# Revit family: V-LENSESxx102xxWSxx
name_source: partatom
category: Leuchten
units: mm (PartAtom-declared; Revit-internal decimal feet)

## family parameters
Basisbauteil = Fläche
Beim Laden mit Abzugskörper schneiden = Nein
Bemaßung runder Anschluss = Durchmesser verwenden
Gemeinsam genutzt = Nein
Lichtquelle = Ja
OmniClass-Nummer = 23.80.70.11
OmniClass-Titel = Luminaries for Internal Lighting
Raumberechnungspunkt = Nein
Teiletyp = Normal

## types (8) — shared parameters
Baugruppenkennzeichen = D5020200
Emissionsform beim Rendern sichtbar = Nein
Farbfilter = 16777215
Farbtemperaturverschiebung bei Dämpfen der Lampe = <Keine Auswahl>
Hersteller = RIDI Leuchten GmbH
Lampe = LED
Neigungswinkel = 90.00°
URL = www.ridi.de
Von Breite des Rechtecks ausssenden = 1018 mm  [stored 3.3399 ft]
Von Länge des Rechtecks aussenden = 111 mm
brand = RIDI
conformity mark = CE
electrical safety class = 1
height = 83 mm  [stored 0.27231 ft]
ingress protection (IP) code = IP20
length = 1024 mm  [stored 3.35958 ft]
nominal frequency = 50-60Hz
nominal voltage = 230
voltage type (AC, DC, UC) = AC
width = 113 mm  [stored 0.370735 ft]
zero-valued in all types: Vorgabe-Ansicht

## per-type parameters (varying)
| type | Datei für fotometrisches Netz | Modell | Scheinlast | product name | rated input power | weight |
| V-LENSES-D102-5RFWS840B0450 | V-LENSES-D.IES | 1522559 | 26 VA | V-LENSES-D102-5RFWS840B0450
V-LENSES-DI102-7DASW830B0550 | 26 | 2,6 |
| V-LENSES-D102-7DAWS830B0350 | V-LENSES-D.IES | 1532563 | 22 VA | V-LENSES-D102-7DAWS830B0350
V-LENSES-DI102-7DASW830B0550 | 22 | 2,6 |
| V-LENSES-D102-7DAWS840B0350 | V-LENSES-D.IES | 1532555 | 22 VA | V-LENSES-D102-7DAWS840B0350
V-LENSES-DI102-7DASW830B0550 | 22 | 2,6 |
| V-LENSES-DI102-5RFWS830B0500 | V-LENSES-DI.IES | 1522568 | 37 VA | V-LENSES-DI102-5RFWS830B0500
V-LENSES-DI102-7DASW830B0550 | 37 | 2,8 |
| V-LENSES-DI102-5RFWS840B0550 | V-LENSES-DI.IES | 1522560 | 37 VA | V-LENSES-DI102-5RFWS840B0550
V-LENSES-DI102-5RFWS840B0550 | 37 | 2,8 |
| V-LENSES-DI102-7DAWS830B0500 | V-LENSES-DI.IES | 1532564 | 32 VA | V-LENSES-DI102-7DAWS830B0500
V-LENSES-DI102-5RFWS840B0550 | 32 | 2,8 |
| V-LENSES-DI102-7DAWS840B0500 | V-LENSES-DI.IES | 1532556 | 32 VA | V-LENSES-DI102-7DAWS840B0500
V-LENSES-DI102-7DAWS840B0500 | 32 | 2,8 |
| V-LENSES-D102-5RFWS830B0450 | V-LENSES-D.IES | 1522567 | 26 VA | V-LENSES-D102-5RFWS830B0450 | 26 | 2,6 |

note: [stored X ft] marks values corroborated as IEEE doubles in the binary element streams (Revit-internal decimal feet)
